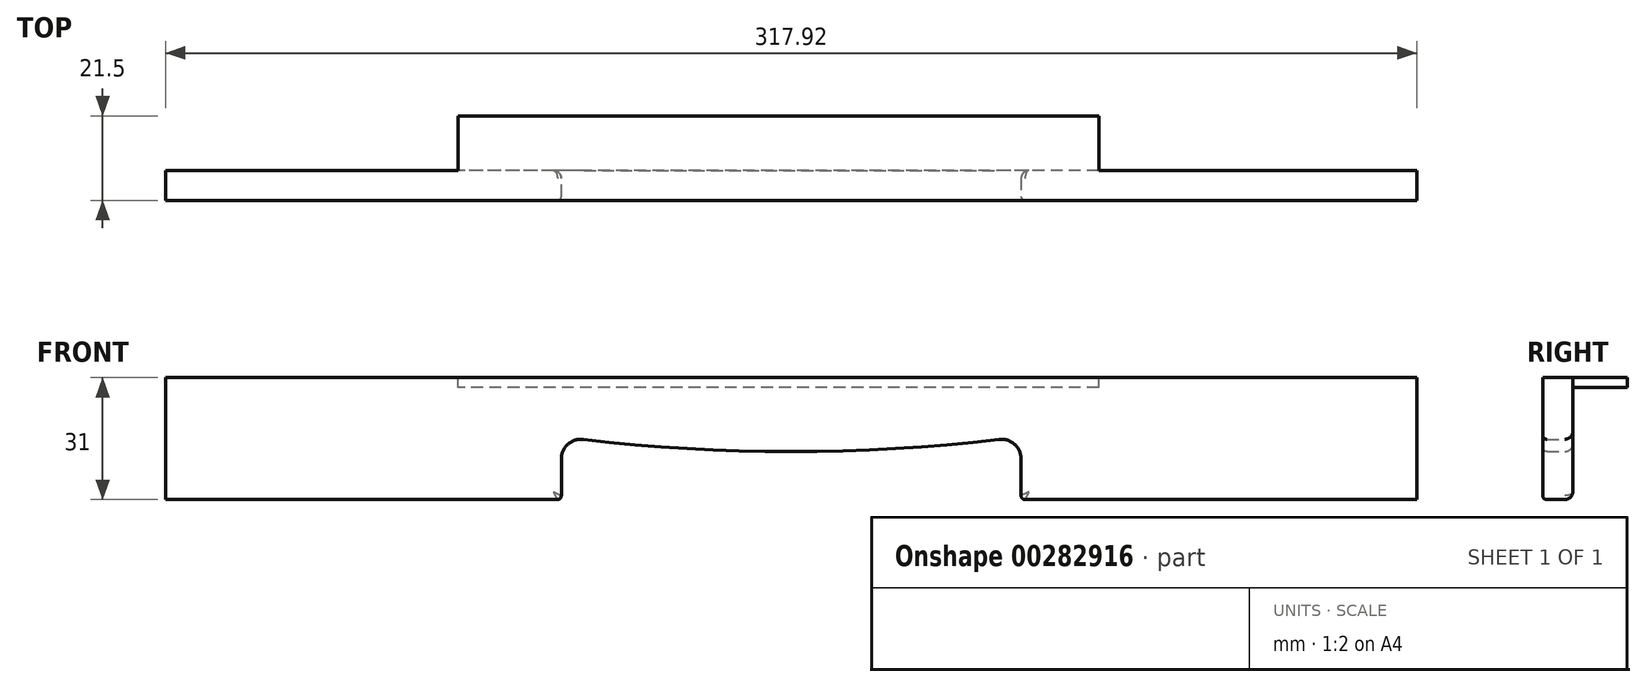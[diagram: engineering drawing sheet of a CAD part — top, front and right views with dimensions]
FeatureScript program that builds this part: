
annotation { "Feature Type Name" : "Feature", "Feature Type Description" : "" }
export const myFeature = defineFeature(function(context is Context, id is Id, definition is map)
    precondition{}
    {
        {
            var Q0;
            Q0=qCreatedBy(makeId("Front.planeOp"),FACE);
            var sketch = newSketch(context, id + "F0", { "sketchPlane" : qUnion([Q0])});
            skArc(sketch, "E0", {"start": v(-58.4, -447.2) * mm, "mid": v(0, -451) * mm, "end": v(58.4, -447.2) * mm});
            skLineSegment(sketch, "E1", {"start": v(-158.96, -432.2) * mm, "end": v(158.96, -432.2) * mm});
            skLineSegment(sketch, "E2", {"start": v(0, 0) * mm, "end": v(0, -650.2) * mm, "construction": true});
            skLineSegment(sketch, "E3", {"start": v(-58.4, -447.2) * mm, "end": v(-58.4, -463.2) * mm});
            skLineSegment(sketch, "E4", {"start": v(58.4, -447.2) * mm, "end": v(58.4, -463.2) * mm});
            skLineSegment(sketch, "E5", {"start": v(158.96, -463.2) * mm, "end": v(58.4, -463.2) * mm});
            skLineSegment(sketch, "E6", {"start": v(-158.96, -463.2) * mm, "end": v(-158.96, -432.2) * mm});
            skLineSegment(sketch, "E7", {"start": v(158.96, -463.2) * mm, "end": v(158.96, -432.2) * mm});
            skLineSegment(sketch, "E8.trimOffspring", {"start": v(-58.4, -463.2) * mm, "end": v(-158.96, -463.2) * mm});
            skSolve(sketch);
        }
        {
            var Q0;
            Q0 = qSketchRegion(id + "F0", true);
            extrude(context, id + "F1", {"entities" : qUnion([Q0]), "depth" : 7.6 * mm});
        }
        {
            var Q0;
            Q0=makeQuery(id+"F1.opExtrude","SWEPT_EDGE",EDGE,{"disambiguationData":[OSD([sQuery(id+"F0.wireOp",EDGE,"E0"),sQuery(id+"F0.wireOp",EDGE,"E3")])]});
            var Q1;
            Q1=makeQuery(id+"F1.opExtrude","SWEPT_EDGE",EDGE,{"disambiguationData":[OSD([sQuery(id+"F0.wireOp",EDGE,"E0"),sQuery(id+"F0.wireOp",EDGE,"E4")])]});
            fillet(context, id + "F2", {"entities" : qUnion([Q0, Q1]), "radius" : 5 * mm, "tangentPropagation" : true, "allowEdgeOverflow" : false});
        }
        {
            var Q0;
            Q0=makeQuery(id+"F1.opExtrude","SWEPT_EDGE",EDGE,{"disambiguationData":[OSD([sQuery(id+"F0.wireOp",EDGE,"E4"),sQuery(id+"F0.wireOp",EDGE,"E5")])]});
            var Q1;
            Q1=makeQuery(id+"F1.opExtrude","SWEPT_EDGE",EDGE,{"disambiguationData":[OSD([sQuery(id+"F0.wireOp",EDGE,"E3"),sQuery(id+"F0.wireOp",EDGE,"E8.trimOffspring")])]});
            fillet(context, id + "F3", {"entities" : qUnion([Q0, Q1]), "radius" : 1 * mm, "tangentPropagation" : true, "allowEdgeOverflow" : false});
        }
        {
            var Q0;
            Q0=makeQuery(id+"F1.opExtrude","CAP_EDGE",EDGE,{"disambiguationData":[OSD([sQuery(id+"F0.wireOp",EDGE,"E0")])],"isStart":false});
            fillet(context, id + "F4", {"entities" : qUnion([Q0]), "radius" : 1 * mm, "tangentPropagation" : true, "allowEdgeOverflow" : false});
        }
        {
            var Q0;
            Q0=makeQuery(id+"F1.opExtrude","CAP_EDGE",EDGE,{"disambiguationData":[OSD([sQuery(id+"F0.wireOp",EDGE,"E0")])],"isStart":true});
            fillet(context, id + "F5", {"entities" : qUnion([Q0]), "radius" : 2 * mm, "tangentPropagation" : true, "allowEdgeOverflow" : false});
        }
        {
            var Q0;
            Q0=makeQuery(id+"F1.opExtrude","CAP_FACE",FACE,{"disambiguationData":[OSD([sQuery(id+"F0.wireOp",EDGE,"E0"),sQuery(id+"F0.wireOp",EDGE,"E1"),sQuery(id+"F0.wireOp",EDGE,"E3"),sQuery(id+"F0.wireOp",EDGE,"E4"),sQuery(id+"F0.wireOp",EDGE,"E5"),sQuery(id+"F0.wireOp",EDGE,"E6"),sQuery(id+"F0.wireOp",EDGE,"E7"),sQuery(id+"F0.wireOp",EDGE,"E8.trimOffspring")])],"isStart":true});
            var sketch = newSketch(context, id + "F6", { "sketchPlane" : qUnion([Q0])});
            skLineSegment(sketch, "E9.0", {"start": v(84.68, -432.2) * mm, "end": v(-78.13, -432.2) * mm});
            skLineSegment(sketch, "E10", {"start": v(-78.13, -434.7) * mm, "end": v(84.68, -434.7) * mm});
            skLineSegment(sketch, "E11", {"start": v(84.68, -434.7) * mm, "end": v(84.68, -432.2) * mm});
            skLineSegment(sketch, "E12", {"start": v(-78.13, -434.7) * mm, "end": v(-78.13, -432.2) * mm});
            skPoint(sketch, "E13.orphan", {"position": v(-158.96, -432.2) * mm});
            skPoint(sketch, "E14.orphan", {"position": v(158.96, -432.2) * mm});
            skSolve(sketch);
        }
        {
            var Q0;
            Q0 = qSketchRegion(id + "F6", true);
            extrude(context, id + "F7", {"entities" : qUnion([Q0]), "operationType" : NewBodyOperationType.ADD, "depth" : 13.9 * mm});
        }
    });
